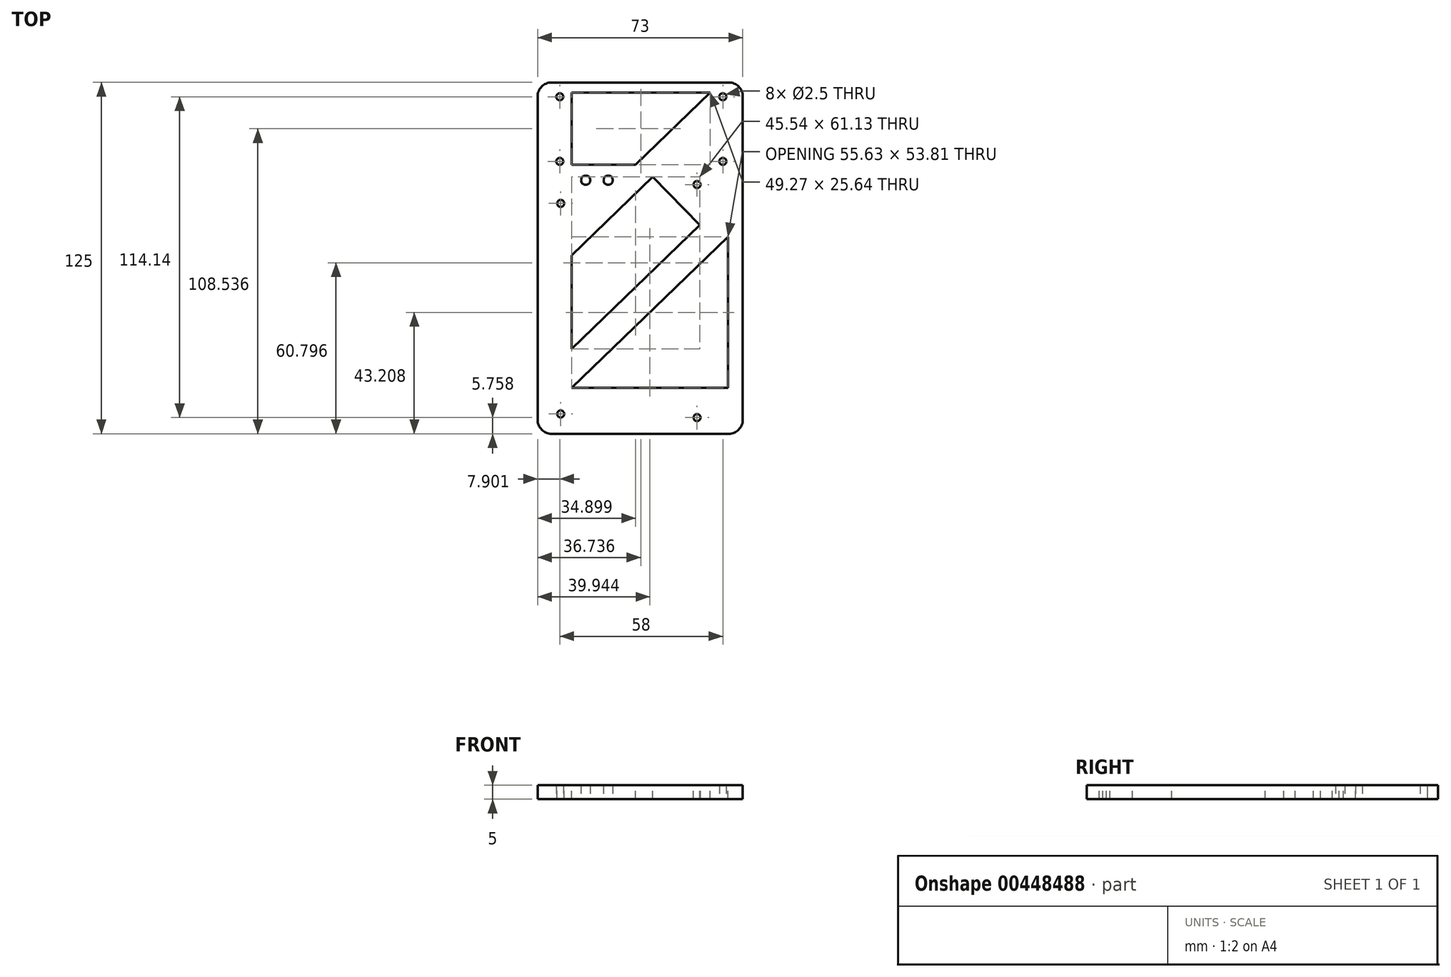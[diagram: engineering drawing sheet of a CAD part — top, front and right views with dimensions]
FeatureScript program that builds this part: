
annotation { "Feature Type Name" : "Feature", "Feature Type Description" : "" }
export const myFeature = defineFeature(function(context is Context, id is Id, definition is map)
    precondition{}
    {
        {
            var Q0;
            Q0=qCreatedBy(makeId("Top.planeOp"),FACE);
            var sketch = newSketch(context, id + "F0", { "sketchPlane" : qUnion([Q0])});
            skPoint(sketch, "E0.middle", {"position": v(0, 0) * mm});
            skLineSegment(sketch, "E1.bottom", {"start": v(34.79, -43.18) * mm, "end": v(-38.21, -43.18) * mm});
            skLineSegment(sketch, "E1.top", {"start": v(34.79, 81.82) * mm, "end": v(-38.21, 81.82) * mm});
            skLineSegment(sketch, "E1.left", {"start": v(34.79, -43.18) * mm, "end": v(34.79, 81.82) * mm});
            skLineSegment(sketch, "E1.right", {"start": v(-38.21, -43.18) * mm, "end": v(-38.21, 81.82) * mm});
            skLineSegment(sketch, "E2", {"start": v(-21.09, 47.03) * mm, "end": v(-13.09, 47.03) * mm, "construction": true});
            skLineSegment(sketch, "E3.bottom", {"start": v(-30.3, 76.72) * mm, "end": v(27.7, 76.72) * mm, "construction": true});
            skLineSegment(sketch, "E3.top", {"start": v(-30.3, 53.72) * mm, "end": v(27.7, 53.72) * mm, "construction": true});
            skLineSegment(sketch, "E3.left", {"start": v(-30.3, 76.72) * mm, "end": v(-30.3, 53.72) * mm, "construction": true});
            skLineSegment(sketch, "E3.right", {"start": v(27.7, 76.72) * mm, "end": v(27.7, 53.72) * mm, "construction": true});
            skSolve(sketch);
        }
        {
            var Q0;
            Q0=qSketchRegion(id+"F0",true);
            extrude(context, id + "F1", {"entities" : qUnion([Q0]), "depth" : 5 * mm, "offsetDistance" : 25 * mm});
        }
        {
            var Q0;
            Q0=sQuery(id+"F0.wireOp",VERTEX,"E3.bottom.start");
            var Q1;
            Q1=sQuery(id+"F0.wireOp",VERTEX,"E3.right.start");
            var Q2;
            Q2=sQuery(id+"F0.wireOp",VERTEX,"E3.right.end");
            var Q3;
            Q3=sQuery(id+"F0.wireOp",VERTEX,"E3.left.end");
            var Q4;
            Q4=makeQuery(id+"F1.opExtrude","SWEPT_BODY",BODY,{"disambiguationData":[OSD([sQuery(id+"F0.wireOp",EDGE,"E1.bottom"),sQuery(id+"F0.wireOp",EDGE,"E1.top"),sQuery(id+"F0.wireOp",EDGE,"E1.left"),sQuery(id+"F0.wireOp",EDGE,"E1.right")])]});
            hole(context, id + "F2", {"style" : HoleStyle.SIMPLE, "endStyle" : HoleEndStyle.THROUGH, "oppositeDirection" : true, "standardTappedOrClearance" : lookupTablePath({ "standard" : "ISO", "engagement" : "75%", "pitch" : "0.5 mm", "size" : "M3", "type" : "Tapped" }), "standardBlindInLast" : lookupTablePath({ "standard" : "ISO", "engagement" : "75%", "pitch" : "0.5 mm", "size" : "M3", "type" : "Tapped" }), "holeDiameter" : 2.5 * mm, "majorDiameter" : 3 * mm, "showTappedDepth" : true, "isTappedThrough" : true, "tappedDepth" : 12 * mm, "tapClearance" : 3, "startFromSketch" : true, "locations" : qUnion([Q0, Q1, Q2, Q3]), "scope" : qUnion([Q4])});
        }
        {
            var Q0;
            Q0=sQuery(id+"F0.wireOp",VERTEX,"E2.start");
            var Q1;
            Q1=sQuery(id+"F0.wireOp",VERTEX,"E2.end");
            var Q2;
            Q2=makeQuery(id+"F1.opExtrude","SWEPT_BODY",BODY,{"disambiguationData":[OSD([sQuery(id+"F0.wireOp",EDGE,"E1.bottom"),sQuery(id+"F0.wireOp",EDGE,"E1.top"),sQuery(id+"F0.wireOp",EDGE,"E1.left"),sQuery(id+"F0.wireOp",EDGE,"E1.right")])]});
            hole(context, id + "F3", {"style" : HoleStyle.SIMPLE, "endStyle" : HoleEndStyle.THROUGH, "oppositeDirection" : true, "standardTappedOrClearance" : lookupTablePath({ "standard" : "ISO", "fit" : "Normal", "size" : "M3", "type" : "Clearance" }), "standardBlindInLast" : lookupTablePath({ "fit" : "Standard", "standard" : "ISO", "size" : "M3", "type" : "Clearance" }), "holeDiameter" : 3.3 * mm, "majorDiameter" : 5 * mm, "isTappedThrough" : true, "tappedDepth" : 12 * mm, "tapClearance" : 3, "startFromSketch" : true, "locations" : qUnion([Q0, Q1]), "scope" : qUnion([Q2])});
        }
        {
            var Q0;
            Q0=makeQuery(id+"F1.opExtrude","SWEPT_EDGE",EDGE,{"disambiguationData":[OSD([sQuery(id+"F0.wireOp",EDGE,"E1.top"),sQuery(id+"F0.wireOp",EDGE,"E1.right")])]});
            var Q1;
            Q1=makeQuery(id+"F1.opExtrude","SWEPT_EDGE",EDGE,{"disambiguationData":[OSD([sQuery(id+"F0.wireOp",EDGE,"E1.top"),sQuery(id+"F0.wireOp",EDGE,"E1.left")])]});
            var Q2;
            Q2=makeQuery(id+"F1.opExtrude","SWEPT_EDGE",EDGE,{"disambiguationData":[OSD([sQuery(id+"F0.wireOp",EDGE,"E1.bottom"),sQuery(id+"F0.wireOp",EDGE,"E1.left")])]});
            var Q3;
            Q3=makeQuery(id+"F1.opExtrude","SWEPT_EDGE",EDGE,{"disambiguationData":[OSD([sQuery(id+"F0.wireOp",EDGE,"E1.bottom"),sQuery(id+"F0.wireOp",EDGE,"E1.right")])]});
            var Q4;
            Q4=makeQuery(id+"F7.boolean.opBoolean","COPY",EDGE,{"derivedFrom":makeQuery(id+"F7.opExtrude","SWEPT_EDGE",EDGE,{"disambiguationData":[OSD([sQuery(id+"F5.wireOp",EDGE,"E12"),sQuery(id+"F5.wireOp",EDGE,"E15")])]})});
            var Q5;
            Q5=makeQuery(id+"F7.boolean.opBoolean","COPY",EDGE,{"derivedFrom":makeQuery(id+"F7.opExtrude","SWEPT_EDGE",EDGE,{"disambiguationData":[OSD([sQuery(id+"F5.wireOp",EDGE,"E15"),sQuery(id+"F5.wireOp",EDGE,"E16")])]})});
            var Q6;
            Q6=makeQuery(id+"F7.boolean.opBoolean","COPY",EDGE,{"derivedFrom":makeQuery(id+"F7.opExtrude","SWEPT_EDGE",EDGE,{"disambiguationData":[OSD([sQuery(id+"F5.wireOp",EDGE,"E6"),sQuery(id+"F5.wireOp",EDGE,"E7")])]})});
            var Q7;
            Q7=makeQuery(id+"F7.boolean.opBoolean","COPY",EDGE,{"derivedFrom":makeQuery(id+"F7.opExtrude","SWEPT_EDGE",EDGE,{"disambiguationData":[OSD([sQuery(id+"F5.wireOp",EDGE,"E4"),sQuery(id+"F5.wireOp",EDGE,"E7")])]})});
            var Q8;
            Q8=makeQuery(id+"F7.boolean.opBoolean","COPY",EDGE,{"derivedFrom":makeQuery(id+"F7.opExtrude","SWEPT_EDGE",EDGE,{"disambiguationData":[OSD([sQuery(id+"F5.wireOp",EDGE,"E9"),sQuery(id+"F5.wireOp",EDGE,"E10")])]})});
            fillet(context, id + "F4", {"entities" : qUnion([Q0, Q1, Q2, Q3, Q4, Q5, Q6, Q7, Q8]), "radius" : 5 * mm, "tangentPropagation" : true, "allowEdgeOverflow" : false});
        }
        {
            var Q0;
            Q0=makeQuery(id+"F1.opExtrude","CAP_FACE",FACE,{"disambiguationData":[OSD([sQuery(id+"F0.wireOp",EDGE,"E1.bottom"),sQuery(id+"F0.wireOp",EDGE,"E1.top"),sQuery(id+"F0.wireOp",EDGE,"E1.left"),sQuery(id+"F0.wireOp",EDGE,"E1.right")])],"isStart":false});
            var sketch = newSketch(context, id + "F5", { "sketchPlane" : qUnion([Q0])});
            skLineSegment(sketch, "E4", {"start": v(2.72, 48.18) * mm, "end": v(-26.08, 20.32) * mm});
            skLineSegment(sketch, "E5", {"start": v(-26.08, 20.32) * mm, "end": v(-26.08, -12.95) * mm});
            skLineSegment(sketch, "E6", {"start": v(-26.08, -12.95) * mm, "end": v(19.46, 31.1) * mm});
            skLineSegment(sketch, "E7", {"start": v(19.46, 31.1) * mm, "end": v(2.72, 48.18) * mm});
            skLineSegment(sketch, "E8", {"start": v(-26.08, -26.88) * mm, "end": v(29.55, 26.94) * mm});
            skLineSegment(sketch, "E9", {"start": v(29.55, 26.94) * mm, "end": v(29.55, -26.88) * mm});
            skLineSegment(sketch, "E10", {"start": v(29.55, -26.88) * mm, "end": v(-26.08, -26.88) * mm});
            skLineSegment(sketch, "E11", {"start": v(23.16, 78.17) * mm, "end": v(-3.34, 52.54) * mm});
            skLineSegment(sketch, "E12", {"start": v(-3.34, 52.54) * mm, "end": v(-26.1, 52.54) * mm});
            skPoint(sketch, "E13.end.orphan", {"position": v(-22.38, 78.17) * mm});
            skPoint(sketch, "E14.start.orphan", {"position": v(0.4, 78.17) * mm});
            skLineSegment(sketch, "E15", {"start": v(-26.1, 52.54) * mm, "end": v(-26.1, 78.17) * mm});
            skLineSegment(sketch, "E16", {"start": v(-26.1, 78.17) * mm, "end": v(23.16, 78.17) * mm});
            skSolve(sketch);
        }
        {
            var Q0;
            Q0=makeQuery(id+"F5.imprint","IMPRINT",FACE,{"disambiguationData":[TD([[makeQuery(id+"F5.imprint","IMPRINT",EDGE,{"derivedFrom":sQuery(id+"F5.wireOp",EDGE,"E4")}),-1.0]])]});
            var sketch = newSketch(context, id + "F6", { "sketchPlane" : qUnion([Q0])});
            skLineSegment(sketch, "E17", {"start": v(-30, 38.78) * mm, "end": v(-30, -36.12) * mm, "construction": true});
            skLineSegment(sketch, "E18", {"start": v(18.5, 45.48) * mm, "end": v(18.5, -37.42) * mm, "construction": true});
            skLineSegment(sketch, "E19", {"start": v(22.78, -36.12) * mm, "end": v(31.63, -36.12) * mm, "construction": true});
            skSolve(sketch);
        }
        {
            var Q0;
            Q0=makeQuery(id+"F5.imprint","IMPRINT",FACE,{"disambiguationData":[TD([[makeQuery(id+"F5.imprint","IMPRINT",EDGE,{"derivedFrom":sQuery(id+"F5.wireOp",EDGE,"E4")}),1.0]])]});
            var Q1;
            Q1=makeQuery(id+"F5.imprint","IMPRINT",FACE,{"disambiguationData":[TD([[makeQuery(id+"F5.imprint","IMPRINT",EDGE,{"derivedFrom":sQuery(id+"F5.wireOp",EDGE,"E8")}),-1.0]])]});
            var Q2;
            Q2=makeQuery(id+"F5.imprint","IMPRINT",FACE,{"disambiguationData":[TD([[makeQuery(id+"F5.imprint","IMPRINT",EDGE,{"derivedFrom":sQuery(id+"F5.wireOp",EDGE,"E14")}),-1.0]])]});
            var Q3;
            Q3=makeQuery(id+"F5.imprint","IMPRINT",FACE,{"disambiguationData":[TD([[makeQuery(id+"F5.imprint","IMPRINT",EDGE,{"derivedFrom":sQuery(id+"F5.wireOp",EDGE,"E11")}),-1.0]])]});
            extrude(context, id + "F7", {"entities" : qUnion([Q0, Q1, Q2, Q3]), "operationType" : NewBodyOperationType.REMOVE, "oppositeDirection" : true, "depth" : 25 * mm, "offsetDistance" : 25 * mm});
        }
        {
            var Q0;
            Q0=sQuery(id+"F6.wireOp",VERTEX,"E17.start");
            var Q1;
            Q1=sQuery(id+"F6.wireOp",VERTEX,"E18.start");
            var Q2;
            Q2=sQuery(id+"F6.wireOp",VERTEX,"E18.end");
            var Q3;
            Q3=sQuery(id+"F6.wireOp",VERTEX,"E17.end");
            var Q4;
            Q4=makeQuery(id+"F1.opExtrude","SWEPT_BODY",BODY,{"disambiguationData":[OSD([sQuery(id+"F0.wireOp",EDGE,"E1.bottom"),sQuery(id+"F0.wireOp",EDGE,"E1.top"),sQuery(id+"F0.wireOp",EDGE,"E1.left"),sQuery(id+"F0.wireOp",EDGE,"E1.right")])]});
            hole(context, id + "F8", {"style" : HoleStyle.SIMPLE, "endStyle" : HoleEndStyle.THROUGH, "standardTappedOrClearance" : lookupTablePath({ "standard" : "ISO", "engagement" : "75%", "pitch" : "0.5 mm", "size" : "M3", "type" : "Tapped" }), "standardBlindInLast" : lookupTablePath({ "standard" : "ISO", "engagement" : "75%", "pitch" : "0.5 mm", "size" : "M3", "type" : "Tapped" }), "holeDiameter" : 2.5 * mm, "majorDiameter" : 3 * mm, "showTappedDepth" : true, "isTappedThrough" : true, "tappedDepth" : 12 * mm, "tapClearance" : 3, "startFromSketch" : true, "locations" : qUnion([Q0, Q1, Q2, Q3]), "scope" : qUnion([Q4])});
        }
    });
